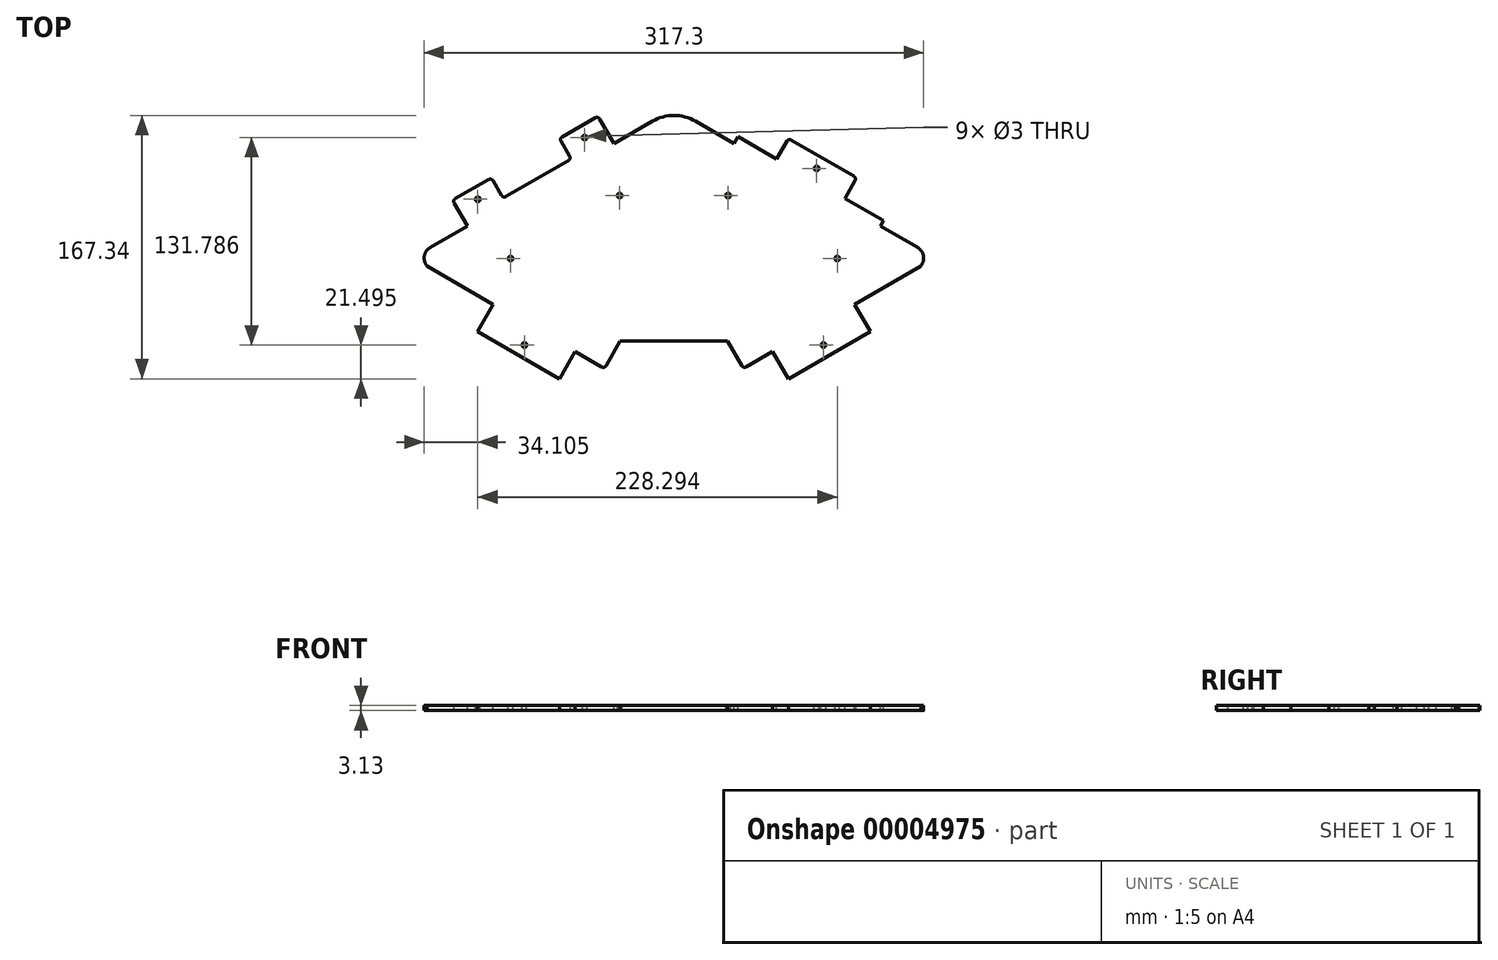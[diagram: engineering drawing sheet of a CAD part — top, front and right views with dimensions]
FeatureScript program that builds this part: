
annotation { "Feature Type Name" : "Feature", "Feature Type Description" : "" }
export const myFeature = defineFeature(function(context is Context, id is Id, definition is map)
    precondition{}
    {
        {
            var Q0;
            Q0=qCreatedBy(makeId("Top.planeOp"),FACE);
            var sketch = newSketch(context, id + "F0", { "sketchPlane" : qUnion([Q0])});
            skLineSegment(sketch, "E0", {"start": v(0, 0) * mm, "end": v(0, 109.98) * mm, "construction": true});
            skLineSegment(sketch, "E1", {"start": v(0, 0) * mm, "end": v(-197.45, 114) * mm});
            skLineSegment(sketch, "E2.0.MirrorCS", {"start": v(0, 0) * mm, "end": v(197.45, 114) * mm});
            skCircle(sketch, "E3", {"center": v(0, 228) * mm, "radius": 197.45 * mm, "construction": true});
            skPoint(sketch, "E4", {"position": v(-98.73, 57) * mm});
            skLineSegment(sketch, "E5", {"start": v(-197.45, 114) * mm, "end": v(0, 228) * mm});
            skLineSegment(sketch, "E6", {"start": v(0, 228) * mm, "end": v(197.45, 114) * mm});
            skSolve(sketch);
        }
        {
            var Q0;
            Q0 = qSketchRegion(id + "F0", true);
            extrude(context, id + "F1", {"entities" : qUnion([Q0]), "depth" : 3.12 * mm});
        }
        {
            var Q0;
            Q0=makeQuery(id+"F1.opExtrude","CAP_FACE",FACE,{"disambiguationData":[OSD([sQuery(id+"F0.wireOp",EDGE,"E1"),sQuery(id+"F0.wireOp",EDGE,"E2.0.MirrorCS"),sQuery(id+"F0.wireOp",EDGE,"E5"),sQuery(id+"F0.wireOp",EDGE,"E6")])],"isStart":false});
            var sketch = newSketch(context, id + "F2", { "sketchPlane" : qUnion([Q0])});
            skLineSegment(sketch, "E7", {"start": v(0, 0) * mm, "end": v(0, 228) * mm, "construction": true});
            skLineSegment(sketch, "E8", {"start": v(-8.66, 5) * mm, "end": v(8.66, 5) * mm});
            skLineSegment(sketch, "E9", {"start": v(8.66, 5) * mm, "end": v(0, 0) * mm});
            skLineSegment(sketch, "E10", {"start": v(-8.66, 5) * mm, "end": v(0, 0) * mm});
            skLineSegment(sketch, "E11", {"start": v(-197.45, 114) * mm, "end": v(-193.12, 116.5) * mm});
            skLineSegment(sketch, "E12", {"start": v(-193.12, 116.5) * mm, "end": v(-188.8, 109) * mm});
            skLineSegment(sketch, "E13", {"start": v(-188.8, 109) * mm, "end": v(-197.45, 114) * mm});
            skLineSegment(sketch, "E14.0.MirrorCS", {"start": v(188.8, 109) * mm, "end": v(197.45, 114) * mm});
            skLineSegment(sketch, "E14.1.MirrorCS", {"start": v(193.12, 116.5) * mm, "end": v(188.8, 109) * mm});
            skLineSegment(sketch, "E14.2.MirrorCS", {"start": v(197.45, 114) * mm, "end": v(193.12, 116.5) * mm});
            skSolve(sketch);
        }
        {
            var Q0;
            Q0 = qSketchRegion(id + "F2", true);
            extrude(context, id + "F3", {"entities" : qUnion([Q0]), "operationType" : NewBodyOperationType.REMOVE, "endBound" : BoundingType.THROUGH_ALL, "oppositeDirection" : true, "depth" : 25 * mm});
        }
        {
            var Q0;
            Q0=makeQuery(id+"F1.opExtrude","CAP_FACE",FACE,{"disambiguationData":[OSD([sQuery(id+"F0.wireOp",EDGE,"E1"),sQuery(id+"F0.wireOp",EDGE,"E2.0.MirrorCS"),sQuery(id+"F0.wireOp",EDGE,"E5"),sQuery(id+"F0.wireOp",EDGE,"E6")])],"isStart":false});
            var sketch = newSketch(context, id + "F4", { "sketchPlane" : qUnion([Q0])});
            skLineSegment(sketch, "E15", {"start": v(0, 0) * mm, "end": v(0, 228) * mm, "construction": true});
            skLineSegment(sketch, "E16", {"start": v(-72.75, 42) * mm, "end": v(-62.75, 59.32) * mm});
            skLineSegment(sketch, "E17", {"start": v(-62.75, 59.32) * mm, "end": v(-44.13, 48.57) * mm});
            skLineSegment(sketch, "E18", {"start": v(-44.13, 48.57) * mm, "end": v(-34.08, 65.98) * mm});
            skLineSegment(sketch, "E19", {"start": v(-72.75, 42) * mm, "end": v(-8.66, 5) * mm});
            skLineSegment(sketch, "E20.0.MirrorCS", {"start": v(72.75, 42) * mm, "end": v(8.66, 5) * mm});
            skLineSegment(sketch, "E20.1.MirrorCS", {"start": v(72.75, 42) * mm, "end": v(62.75, 59.32) * mm});
            skLineSegment(sketch, "E20.2.MirrorCS", {"start": v(62.75, 59.32) * mm, "end": v(44.13, 48.57) * mm});
            skLineSegment(sketch, "E20.3.MirrorCS", {"start": v(44.13, 48.57) * mm, "end": v(34.08, 65.98) * mm});
            skLineSegment(sketch, "E21", {"start": v(-34.08, 65.98) * mm, "end": v(34.08, 65.98) * mm});
            skLineSegment(sketch, "E22", {"start": v(-8.66, 5) * mm, "end": v(8.66, 5) * mm});
            skLineSegment(sketch, "E23", {"start": v(-188.8, 109) * mm, "end": v(-124.7, 72) * mm});
            skLineSegment(sketch, "E24", {"start": v(-124.7, 72) * mm, "end": v(-114.7, 89.32) * mm});
            skLineSegment(sketch, "E25", {"start": v(-114.7, 89.32) * mm, "end": v(-156.82, 113.63) * mm});
            skLineSegment(sketch, "E26", {"start": v(-136.83, 149) * mm, "end": v(-131.08, 139.04) * mm});
            skLineSegment(sketch, "E27", {"start": v(-131.08, 139.04) * mm, "end": v(-154.9, 125.3) * mm});
            skLineSegment(sketch, "E28.0", {"start": v(-193.12, 116.5) * mm, "end": v(-188.8, 109) * mm});
            skLineSegment(sketch, "E29", {"start": v(-193.12, 116.5) * mm, "end": v(-136.83, 149) * mm});
            skArc(sketch, "E30", {"start": v(-154.9, 125.3) * mm, "mid": v(-158.4, 120.72) * mm, "end": v(-157.63, 115.02) * mm});
            skLineSegment(sketch, "E31", {"start": v(-157.63, 115.02) * mm, "end": v(-156.82, 113.63) * mm});
            skLineSegment(sketch, "E32.0.MirrorCS", {"start": v(157.63, 115.02) * mm, "end": v(156.82, 113.63) * mm});
            skArc(sketch, "E32.1.MirrorCS", {"start": v(154.9, 125.3) * mm, "mid": v(158.4, 120.72) * mm, "end": v(157.63, 115.02) * mm});
            skLineSegment(sketch, "E32.2.MirrorCS", {"start": v(114.7, 89.32) * mm, "end": v(156.82, 113.63) * mm});
            skLineSegment(sketch, "E32.3.MirrorCS", {"start": v(124.7, 72) * mm, "end": v(114.7, 89.32) * mm});
            skLineSegment(sketch, "E32.4.MirrorCS", {"start": v(188.8, 109) * mm, "end": v(124.7, 72) * mm});
            skLineSegment(sketch, "E32.5.MirrorCS", {"start": v(193.12, 116.5) * mm, "end": v(188.8, 109) * mm});
            skLineSegment(sketch, "E32.6.MirrorCS", {"start": v(131.08, 139.04) * mm, "end": v(154.9, 125.3) * mm});
            skLineSegment(sketch, "E32.7.MirrorCS", {"start": v(136.83, 149) * mm, "end": v(131.08, 139.04) * mm});
            skLineSegment(sketch, "E32.8.MirrorCS", {"start": v(193.12, 116.5) * mm, "end": v(136.83, 149) * mm});
            skLineSegment(sketch, "E33", {"start": v(-44.38, 202.38) * mm, "end": v(0, 228) * mm});
            skLineSegment(sketch, "E34", {"start": v(-44.38, 202.38) * mm, "end": v(-38.13, 191.55) * mm});
            skLineSegment(sketch, "E35", {"start": v(-38.13, 191.55) * mm, "end": v(-13.67, 205.67) * mm});
            skCircle(sketch, "E36", {"center": v(0, 228) * mm, "radius": 6.25 * mm, "construction": true});
            skPoint(sketch, "E37", {"position": v(-5.41, 224.88) * mm});
            skLineSegment(sketch, "E38.0.MirrorCS", {"start": v(38.13, 191.55) * mm, "end": v(13.67, 205.67) * mm});
            skLineSegment(sketch, "E38.1.MirrorCS", {"start": v(44.38, 202.38) * mm, "end": v(38.13, 191.55) * mm});
            skLineSegment(sketch, "E38.2.MirrorCS", {"start": v(44.38, 202.38) * mm, "end": v(0, 228) * mm});
            skArc(sketch, "E39", {"start": v(13.67, 205.67) * mm, "mid": v(0, 209.34) * mm, "end": v(-13.67, 205.67) * mm});
            skSolve(sketch);
        }
        {
            var Q0;
            Q0 = qSketchRegion(id + "F4", true);
            extrude(context, id + "F5", {"entities" : qUnion([Q0]), "operationType" : NewBodyOperationType.REMOVE, "endBound" : BoundingType.THROUGH_ALL, "oppositeDirection" : true, "depth" : 25 * mm});
        }
        {
            var Q0;
            Q0=makeQuery(id+"F1.opExtrude","CAP_FACE",FACE,{"disambiguationData":[OSD([sQuery(id+"F0.wireOp",EDGE,"E1"),sQuery(id+"F0.wireOp",EDGE,"E2.0.MirrorCS"),sQuery(id+"F0.wireOp",EDGE,"E5"),sQuery(id+"F0.wireOp",EDGE,"E6")])],"isStart":false});
            var sketch = newSketch(context, id + "F6", { "sketchPlane" : qUnion([Q0])});
            skLineSegment(sketch, "E40", {"start": v(-90.6, 175.69) * mm, "end": v(-61.5, 125.28) * mm, "construction": true});
            skLineSegment(sketch, "E41", {"start": v(-112.26, 163.19) * mm, "end": v(-68.96, 188.19) * mm});
            skLineSegment(sketch, "E42", {"start": v(-68.96, 188.19) * mm, "end": v(-65.2, 181.7) * mm});
            skLineSegment(sketch, "E43", {"start": v(-65.2, 181.7) * mm, "end": v(-108.5, 156.7) * mm});
            skLineSegment(sketch, "E44", {"start": v(-108.5, 156.7) * mm, "end": v(-112.26, 163.19) * mm});
            skLineSegment(sketch, "E45", {"start": v(90.6, 175.69) * mm, "end": v(65.19, 131.66) * mm, "construction": true});
            skLineSegment(sketch, "E46", {"start": v(44.38, 202.38) * mm, "end": v(40.63, 195.88) * mm});
            skLineSegment(sketch, "E47", {"start": v(40.63, 195.88) * mm, "end": v(65.2, 181.7) * mm});
            skLineSegment(sketch, "E48", {"start": v(65.2, 181.7) * mm, "end": v(68.96, 188.19) * mm});
            skLineSegment(sketch, "E49", {"start": v(68.96, 188.19) * mm, "end": v(44.38, 202.38) * mm});
            skLineSegment(sketch, "E50.0.MirrorCS", {"start": v(136.83, 149) * mm, "end": v(133.08, 142.5) * mm});
            skLineSegment(sketch, "E50.1.MirrorCS", {"start": v(133.08, 142.5) * mm, "end": v(108.5, 156.7) * mm});
            skLineSegment(sketch, "E50.2.MirrorCS", {"start": v(112.26, 163.19) * mm, "end": v(136.83, 149) * mm});
            skLineSegment(sketch, "E50.3.MirrorCS", {"start": v(108.5, 156.7) * mm, "end": v(112.26, 163.19) * mm});
            skSolve(sketch);
        }
        {
            var Q0;
            Q0 = qSketchRegion(id + "F6", true);
            extrude(context, id + "F7", {"entities" : qUnion([Q0]), "operationType" : NewBodyOperationType.REMOVE, "endBound" : BoundingType.THROUGH_ALL, "oppositeDirection" : true, "depth" : 25 * mm});
        }
        {
            var Q0;
            Q0=makeQuery(id+"F1.opExtrude","CAP_FACE",FACE,{"disambiguationData":[OSD([sQuery(id+"F0.wireOp",EDGE,"E1"),sQuery(id+"F0.wireOp",EDGE,"E2.0.MirrorCS"),sQuery(id+"F0.wireOp",EDGE,"E5"),sQuery(id+"F0.wireOp",EDGE,"E6")])],"isStart":false});
            var sketch = newSketch(context, id + "F8", { "sketchPlane" : qUnion([Q0])});
            skLineSegment(sketch, "E51", {"start": v(90.6, 175.69) * mm, "end": v(63.3, 128.4) * mm, "construction": true});
            skLineSegment(sketch, "E52.0", {"start": v(-136.83, 149) * mm, "end": v(-112.26, 163.19) * mm});
            skLineSegment(sketch, "E52.1", {"start": v(-68.96, 188.19) * mm, "end": v(-44.38, 202.38) * mm});
            skLineSegment(sketch, "E53", {"start": v(-136.83, 149) * mm, "end": v(-140.58, 155.5) * mm});
            skLineSegment(sketch, "E54", {"start": v(-140.58, 155.5) * mm, "end": v(-116, 169.68) * mm});
            skLineSegment(sketch, "E55", {"start": v(-116, 169.68) * mm, "end": v(-112.26, 163.19) * mm});
            skLineSegment(sketch, "E56", {"start": v(-44.38, 202.38) * mm, "end": v(-48.13, 208.87) * mm});
            skLineSegment(sketch, "E57", {"start": v(-48.13, 208.87) * mm, "end": v(-72.7, 194.68) * mm});
            skLineSegment(sketch, "E58", {"start": v(-72.7, 194.68) * mm, "end": v(-68.96, 188.19) * mm});
            skLineSegment(sketch, "E59.0", {"start": v(68.96, 188.19) * mm, "end": v(112.26, 163.19) * mm});
            skLineSegment(sketch, "E60", {"start": v(68.96, 188.19) * mm, "end": v(72.7, 194.68) * mm});
            skLineSegment(sketch, "E61", {"start": v(72.7, 194.68) * mm, "end": v(116, 169.68) * mm});
            skLineSegment(sketch, "E62", {"start": v(116, 169.68) * mm, "end": v(112.26, 163.19) * mm});
            skSolve(sketch);
        }
        {
            var Q0;
            Q0 = qSketchRegion(id + "F8", true);
            var Q1;
            Q1=makeQuery(id+"F1.opExtrude","CAP_FACE",FACE,{"disambiguationData":[OSD([sQuery(id+"F0.wireOp",EDGE,"E1"),sQuery(id+"F0.wireOp",EDGE,"E2.0.MirrorCS"),sQuery(id+"F0.wireOp",EDGE,"E5"),sQuery(id+"F0.wireOp",EDGE,"E6")])],"isStart":true});
            extrude(context, id + "F9", {"entities" : qUnion([Q0]), "operationType" : NewBodyOperationType.ADD, "endBound" : BoundingType.UP_TO_SURFACE, "oppositeDirection" : true, "endBoundEntityFace" : qUnion([Q1]), "depth" : 25 * mm});
        }
        {
            var Q0;
            Q0=makeQuery(id+"F9.opExtrude","SWEPT_EDGE",EDGE,{"disambiguationData":[OSD([sQuery(id+"F8.wireOp",EDGE,"E54"),sQuery(id+"F8.wireOp",EDGE,"E55")])]});
            var Q1;
            Q1=makeQuery(id+"F9.opExtrude","SWEPT_EDGE",EDGE,{"disambiguationData":[OSD([sQuery(id+"F8.wireOp",EDGE,"E57"),sQuery(id+"F8.wireOp",EDGE,"E58")])]});
            var Q2;
            Q2=makeQuery(id+"F9.opExtrude","SWEPT_EDGE",EDGE,{"disambiguationData":[OSD([sQuery(id+"F8.wireOp",EDGE,"E53"),sQuery(id+"F8.wireOp",EDGE,"E54")])]});
            var Q3;
            Q3=makeQuery(id+"F9.opExtrude","SWEPT_EDGE",EDGE,{"disambiguationData":[OSD([sQuery(id+"F8.wireOp",EDGE,"E56"),sQuery(id+"F8.wireOp",EDGE,"E57")])]});
            var Q4;
            Q4=makeQuery(id+"F7.boolean.opBoolean","COPY",EDGE,{"derivedFrom":makeQuery(id+"F7.opExtrude","SWEPT_EDGE",EDGE,{"disambiguationData":[OSD([sQuery(id+"F6.wireOp",EDGE,"E42"),sQuery(id+"F6.wireOp",EDGE,"E43")])]})});
            var Q5;
            Q5=makeQuery(id+"F7.boolean.opBoolean","COPY",EDGE,{"derivedFrom":makeQuery(id+"F7.opExtrude","SWEPT_EDGE",EDGE,{"disambiguationData":[OSD([sQuery(id+"F6.wireOp",EDGE,"E43"),sQuery(id+"F6.wireOp",EDGE,"E44")])]})});
            var Q6;
            Q6=makeQuery(id+"F9.opExtrude","SWEPT_EDGE",EDGE,{"disambiguationData":[OSD([sQuery(id+"F8.wireOp",EDGE,"E60"),sQuery(id+"F8.wireOp",EDGE,"E61")])]});
            var Q7;
            Q7=makeQuery(id+"F9.opExtrude","SWEPT_EDGE",EDGE,{"disambiguationData":[OSD([sQuery(id+"F8.wireOp",EDGE,"E61"),sQuery(id+"F8.wireOp",EDGE,"E62")])]});
            var Q8;
            Q8=makeQuery(id+"F5.boolean.opBoolean","COPY",EDGE,{"derivedFrom":makeQuery(id+"F5.opExtrude","SWEPT_EDGE",EDGE,{"disambiguationData":[OSD([sQuery(id+"F0.wireOp",EDGE,"E2.0.MirrorCS"),sQuery(id+"F4.wireOp",EDGE,"E20.0.MirrorCS"),sQuery(id+"F4.wireOp",EDGE,"E20.1.MirrorCS")])]})});
            var Q9;
            Q9=makeQuery(id+"F5.boolean.opBoolean","COPY",EDGE,{"derivedFrom":makeQuery(id+"F5.opExtrude","SWEPT_EDGE",EDGE,{"disambiguationData":[OSD([sQuery(id+"F0.wireOp",EDGE,"E2.0.MirrorCS"),sQuery(id+"F4.wireOp",EDGE,"E32.3.MirrorCS"),sQuery(id+"F4.wireOp",EDGE,"E32.4.MirrorCS")])]})});
            var Q10;
            Q10=makeQuery(id+"F5.boolean.opBoolean","COPY",EDGE,{"derivedFrom":makeQuery(id+"F5.opExtrude","SWEPT_EDGE",EDGE,{"disambiguationData":[OSD([sQuery(id+"F0.wireOp",EDGE,"E1"),sQuery(id+"F4.wireOp",EDGE,"E23"),sQuery(id+"F4.wireOp",EDGE,"E24")])]})});
            var Q11;
            Q11=makeQuery(id+"F5.boolean.opBoolean","COPY",EDGE,{"derivedFrom":makeQuery(id+"F5.opExtrude","SWEPT_EDGE",EDGE,{"disambiguationData":[OSD([sQuery(id+"F0.wireOp",EDGE,"E1"),sQuery(id+"F4.wireOp",EDGE,"E16"),sQuery(id+"F4.wireOp",EDGE,"E19")])]})});
            var Q12;
            Q12=makeQuery(id+"F5.boolean.opBoolean","COPY",EDGE,{"derivedFrom":makeQuery(id+"F5.opExtrude","SWEPT_EDGE",EDGE,{"disambiguationData":[OSD([sQuery(id+"F4.wireOp",EDGE,"E17"),sQuery(id+"F4.wireOp",EDGE,"E18")])]})});
            var Q13;
            Q13=makeQuery(id+"F5.boolean.opBoolean","COPY",EDGE,{"derivedFrom":makeQuery(id+"F5.opExtrude","SWEPT_EDGE",EDGE,{"disambiguationData":[OSD([sQuery(id+"F4.wireOp",EDGE,"E20.2.MirrorCS"),sQuery(id+"F4.wireOp",EDGE,"E20.3.MirrorCS")])]})});
            var Q14;
            Q14=makeQuery(id+"F7.boolean.opBoolean","COPY",EDGE,{"derivedFrom":makeQuery(id+"F7.opExtrude","SWEPT_EDGE",EDGE,{"disambiguationData":[OSD([sQuery(id+"F4.wireOp",EDGE,"E38.1.MirrorCS"),sQuery(id+"F6.wireOp",EDGE,"E46"),sQuery(id+"F6.wireOp",EDGE,"E47")])]})});
            var Q15;
            Q15=makeQuery(id+"F7.boolean.opBoolean","COPY",EDGE,{"derivedFrom":makeQuery(id+"F7.opExtrude","SWEPT_EDGE",EDGE,{"disambiguationData":[OSD([sQuery(id+"F4.wireOp",EDGE,"E32.7.MirrorCS"),sQuery(id+"F6.wireOp",EDGE,"E50.0.MirrorCS"),sQuery(id+"F6.wireOp",EDGE,"E50.1.MirrorCS")])]})});
            fillet(context, id + "F10", {"entities" : qUnion([Q0, Q1, Q2, Q3, Q4, Q5, Q6, Q7, Q8, Q9, Q10, Q11, Q12, Q13, Q14, Q15]), "radius" : 2 * mm, "tangentPropagation" : true, "allowEdgeOverflow" : false});
        }
        {
            var Q0;
            Q0=makeQuery(id+"F9.boolean.opBoolean","MERGE",FACE,{"derivedFrom":[makeQuery(id+"F1.opExtrude","CAP_FACE",FACE,{"disambiguationData":[OSD([sQuery(id+"F0.wireOp",EDGE,"E1"),sQuery(id+"F0.wireOp",EDGE,"E2.0.MirrorCS"),sQuery(id+"F0.wireOp",EDGE,"E5"),sQuery(id+"F0.wireOp",EDGE,"E6")])],"isStart":false}),makeQuery(id+"F9.opExtrude","CAP_FACE",FACE,{"disambiguationData":[OSD([sQuery(id+"F8.wireOp",EDGE,"E52.0"),sQuery(id+"F8.wireOp",EDGE,"E53"),sQuery(id+"F8.wireOp",EDGE,"E54"),sQuery(id+"F8.wireOp",EDGE,"E55")])],"isStart":true}),makeQuery(id+"F9.opExtrude","CAP_FACE",FACE,{"disambiguationData":[OSD([sQuery(id+"F8.wireOp",EDGE,"E52.1"),sQuery(id+"F8.wireOp",EDGE,"E56"),sQuery(id+"F8.wireOp",EDGE,"E57"),sQuery(id+"F8.wireOp",EDGE,"E58")])],"isStart":true}),makeQuery(id+"F9.opExtrude","CAP_FACE",FACE,{"disambiguationData":[OSD([sQuery(id+"F8.wireOp",EDGE,"E59.0"),sQuery(id+"F8.wireOp",EDGE,"E60"),sQuery(id+"F8.wireOp",EDGE,"E61"),sQuery(id+"F8.wireOp",EDGE,"E62")])],"isStart":true})]});
            var sketch = newSketch(context, id + "F11", { "sketchPlane" : qUnion([Q0])});
            skLineSegment(sketch, "E63", {"start": v(-120.96, 78.5) * mm, "end": v(-69, 48.5) * mm, "construction": true});
            skCircle(sketch, "E64", {"center": v(-94.98, 63.5) * mm, "radius": 1.5 * mm});
            skLineSegment(sketch, "E65", {"start": v(0, 0) * mm, "end": v(0, 107.54) * mm, "construction": true});
            skLineSegment(sketch, "E66", {"start": v(-112.26, 163.19) * mm, "end": v(-68.96, 188.19) * mm, "construction": true});
            skLineSegment(sketch, "E67", {"start": v(-68.96, 188.19) * mm, "end": v(-44.38, 202.38) * mm, "construction": true});
            skCircle(sketch, "E68", {"center": v(-90.6, 175.69) * mm, "radius": 1.5 * mm, "construction": true});
            skCircle(sketch, "E69", {"center": v(-56.67, 195.28) * mm, "radius": 1.5 * mm});
            skLineSegment(sketch, "E70", {"start": v(-90.6, 175.69) * mm, "end": v(-62.88, 127.67) * mm, "construction": true});
            skCircle(sketch, "E71.0.MirrorC", {"center": v(-124.55, 156.1) * mm, "radius": 1.5 * mm});
            skCircle(sketch, "E72.0.MirrorC", {"center": v(94.98, 63.5) * mm, "radius": 1.5 * mm});
            skCircle(sketch, "E72.1.MirrorC", {"center": v(56.67, 195.28) * mm, "radius": 1.5 * mm, "construction": true});
            skCircle(sketch, "E72.2.MirrorC", {"center": v(90.6, 175.69) * mm, "radius": 1.5 * mm});
            skCircle(sketch, "E72.3.MirrorC", {"center": v(124.55, 156.1) * mm, "radius": 1.5 * mm, "construction": true});
            skSolve(sketch);
        }
        {
            var Q0;
            Q0 = qSketchRegion(id + "F11", true);
            extrude(context, id + "F12", {"entities" : qUnion([Q0]), "operationType" : NewBodyOperationType.REMOVE, "endBound" : BoundingType.THROUGH_ALL, "oppositeDirection" : true, "depth" : 25 * mm});
        }
        {
            var Q0;
            Q0=makeQuery(id+"F9.boolean.opBoolean","MERGE",FACE,{"derivedFrom":[makeQuery(id+"F1.opExtrude","CAP_FACE",FACE,{"disambiguationData":[OSD([sQuery(id+"F0.wireOp",EDGE,"E1"),sQuery(id+"F0.wireOp",EDGE,"E2.0.MirrorCS"),sQuery(id+"F0.wireOp",EDGE,"E5"),sQuery(id+"F0.wireOp",EDGE,"E6")])],"isStart":false}),makeQuery(id+"F9.opExtrude","CAP_FACE",FACE,{"disambiguationData":[OSD([sQuery(id+"F8.wireOp",EDGE,"E52.0"),sQuery(id+"F8.wireOp",EDGE,"E53"),sQuery(id+"F8.wireOp",EDGE,"E54"),sQuery(id+"F8.wireOp",EDGE,"E55")])],"isStart":true}),makeQuery(id+"F9.opExtrude","CAP_FACE",FACE,{"disambiguationData":[OSD([sQuery(id+"F8.wireOp",EDGE,"E52.1"),sQuery(id+"F8.wireOp",EDGE,"E56"),sQuery(id+"F8.wireOp",EDGE,"E57"),sQuery(id+"F8.wireOp",EDGE,"E58")])],"isStart":true}),makeQuery(id+"F9.opExtrude","CAP_FACE",FACE,{"disambiguationData":[OSD([sQuery(id+"F8.wireOp",EDGE,"E59.0"),sQuery(id+"F8.wireOp",EDGE,"E60"),sQuery(id+"F8.wireOp",EDGE,"E61"),sQuery(id+"F8.wireOp",EDGE,"E62")])],"isStart":true})]});
            var sketch = newSketch(context, id + "F13", { "sketchPlane" : qUnion([Q0])});
            skLineSegment(sketch, "E73", {"start": v(0, 0) * mm, "end": v(0, 182) * mm, "construction": true});
            skLineSegment(sketch, "E74", {"start": v(90.6, 175.69) * mm, "end": v(47.3, 200.7) * mm, "construction": true});
            skLineSegment(sketch, "E75", {"start": v(90.6, 175.69) * mm, "end": v(69.1, 138.45) * mm, "construction": true});
            skLineSegment(sketch, "E76", {"start": v(69.1, 138.45) * mm, "end": v(34.47, 158.45) * mm, "construction": true});
            skCircle(sketch, "E77", {"center": v(34.47, 158.45) * mm, "radius": 1.5 * mm});
            skCircle(sketch, "E78.0.MirrorC", {"center": v(103.75, 118.45) * mm, "radius": 1.5 * mm});
            skCircle(sketch, "E79.0.MirrorC", {"center": v(-103.75, 118.45) * mm, "radius": 1.5 * mm});
            skCircle(sketch, "E79.1.MirrorC", {"center": v(-34.47, 158.45) * mm, "radius": 1.5 * mm});
            skSolve(sketch);
        }
        {
            var Q0;
            Q0 = qSketchRegion(id + "F13", true);
            extrude(context, id + "F14", {"entities" : qUnion([Q0]), "operationType" : NewBodyOperationType.REMOVE, "endBound" : BoundingType.THROUGH_ALL, "oppositeDirection" : true, "depth" : 25 * mm});
        }
    });
